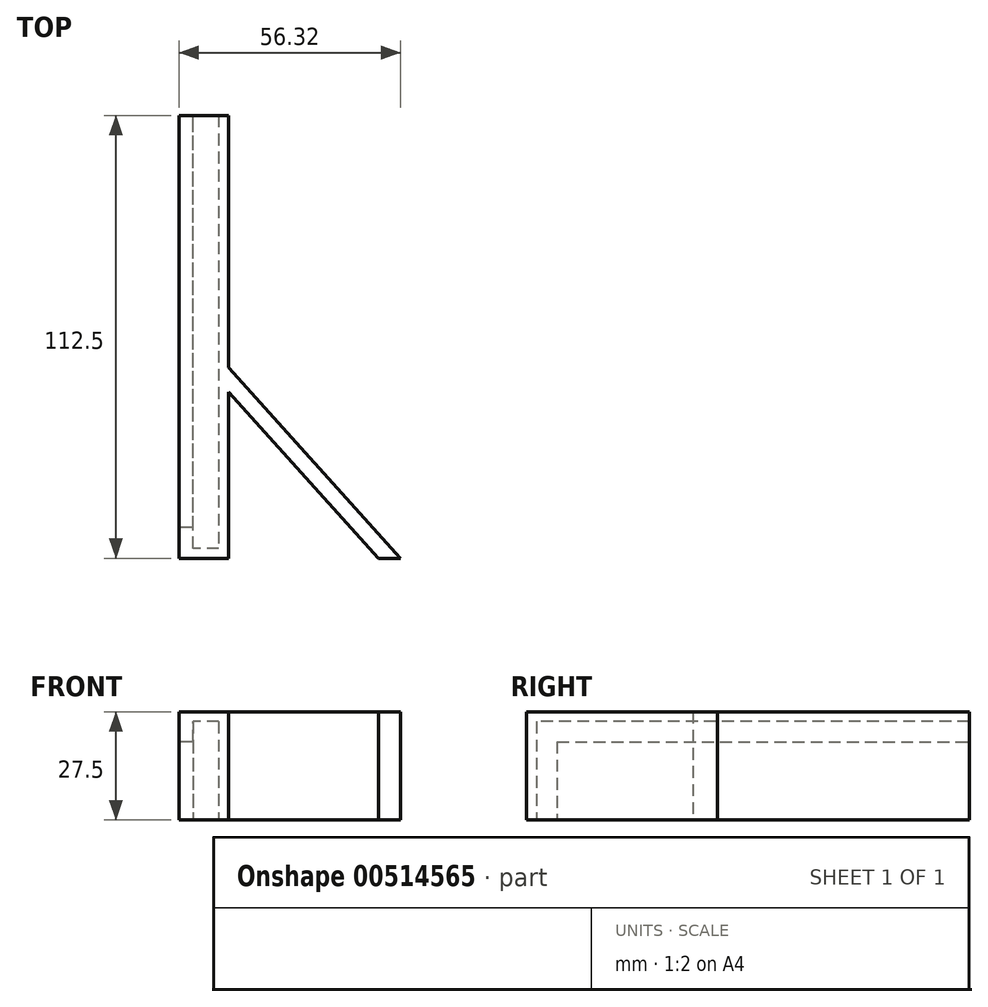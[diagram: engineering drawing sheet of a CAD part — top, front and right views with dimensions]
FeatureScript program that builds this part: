
annotation { "Feature Type Name" : "Feature", "Feature Type Description" : "" }
export const myFeature = defineFeature(function(context is Context, id is Id, definition is map)
    precondition{}
    {
        {
            var Q0;
            Q0=qCreatedBy(makeId("Top.planeOp"),FACE);
            var sketch = newSketch(context, id + "F0", { "sketchPlane" : qUnion([Q0])});
            skLineSegment(sketch, "E0", {"start": v(-21.92, -50.04) * mm, "end": v(-25.53, -50.04) * mm});
            skLineSegment(sketch, "E1", {"start": v(-25.53, -50.04) * mm, "end": v(-25.53, -57.84) * mm});
            skLineSegment(sketch, "E2", {"start": v(-25.53, -57.84) * mm, "end": v(-12.92, -57.84) * mm});
            skLineSegment(sketch, "E3", {"start": v(-12.92, -57.84) * mm, "end": v(-12.92, 34.29) * mm});
            skLineSegment(sketch, "E4", {"start": v(-12.92, 34.29) * mm, "end": v(-12.92, 54.66) * mm});
            skLineSegment(sketch, "E5", {"start": v(-12.92, 54.66) * mm, "end": v(-15.42, 54.66) * mm});
            skLineSegment(sketch, "E6", {"start": v(-15.42, 54.66) * mm, "end": v(-15.42, -55.34) * mm});
            skLineSegment(sketch, "E7", {"start": v(-15.42, -55.34) * mm, "end": v(-21.45, -55.34) * mm});
            skLineSegment(sketch, "E8", {"start": v(-21.45, -55.34) * mm, "end": v(-21.92, -55.34) * mm});
            skLineSegment(sketch, "E9", {"start": v(-21.92, -55.34) * mm, "end": v(-21.92, -50.04) * mm});
            skLineSegment(sketch, "E10", {"start": v(-12.92, -9.37) * mm, "end": v(30.79, -57.84) * mm});
            skLineSegment(sketch, "E11", {"start": v(30.79, -57.84) * mm, "end": v(25.16, -57.84) * mm});
            skLineSegment(sketch, "E12", {"start": v(25.16, -57.84) * mm, "end": v(-12.92, -15.62) * mm});
            skSolve(sketch);
        }
        {
            var Q0;
            Q0=makeQuery(id+"F0.imprint","IMPRINT",FACE,{"disambiguationData":[TD([[makeQuery(id+"F0.imprint","IMPRINT",EDGE,{"derivedFrom":sQuery(id+"F0.wireOp",EDGE,"E0")}),1.0]])]});
            var Q1;
            {var subQ0=sQuery(id+"F0.wireOp",EDGE,"E10");Q1=makeQuery(id+"F0.imprint","IMPRINT",FACE,{"disambiguationData":[TD([[makeQuery(id+"F0.imprint","IMPRINT",EDGE,{"derivedFrom":subQ0}),-1.0]])]});}
            extrude(context, id + "F1", {"entities" : qUnion([Q0, Q1]), "depth" : 25 * mm});
        }
        {
            var Q0;
            Q0=makeQuery(id+"F1.opExtrude","CAP_FACE",FACE,{"disambiguationData":[OSD([sQuery(id+"F0.wireOp",EDGE,"E0"),sQuery(id+"F0.wireOp",EDGE,"E1"),sQuery(id+"F0.wireOp",EDGE,"E2"),sQuery(id+"F0.wireOp",EDGE,"E3"),sQuery(id+"F0.wireOp",EDGE,"E4"),sQuery(id+"F0.wireOp",EDGE,"E5"),sQuery(id+"F0.wireOp",EDGE,"E6"),sQuery(id+"F0.wireOp",EDGE,"E7"),sQuery(id+"F0.wireOp",EDGE,"E8"),sQuery(id+"F0.wireOp",EDGE,"E9"),sQuery(id+"F0.wireOp",EDGE,"E10"),sQuery(id+"F0.wireOp",EDGE,"E11"),sQuery(id+"F0.wireOp",EDGE,"E12")])],"isStart":false});
            var sketch = newSketch(context, id + "F2", { "sketchPlane" : qUnion([Q0])});
            skLineSegment(sketch, "E13.bottom", {"start": v(-12.92, 54.66) * mm, "end": v(-25.53, 54.66) * mm});
            skLineSegment(sketch, "E13.top", {"start": v(-12.92, -57.84) * mm, "end": v(-25.53, -57.84) * mm});
            skLineSegment(sketch, "E13.left", {"start": v(-12.92, 54.66) * mm, "end": v(-12.92, -57.84) * mm});
            skLineSegment(sketch, "E13.right", {"start": v(-25.53, 54.66) * mm, "end": v(-25.53, -57.84) * mm});
            skSolve(sketch);
        }
        {
            var Q0;
            {var subQ1=makeQuery(id+"F1.opExtrude","CAP_EDGE",EDGE,{"disambiguationData":[OSD([sQuery(id+"F0.wireOp",EDGE,"E0")])],"isStart":false});Q0=makeQuery(id+"F2.imprint","IMPRINT",FACE,{"disambiguationData":[TD([[makeQuery(id+"F2.imprint","IMPRINT",EDGE,{"derivedFrom":subQ1}),-1.0]])]});}
            var Q1;
            {var subQ4=sQuery(id+"F2.wireOp",EDGE,"E13.top");Q1=makeQuery(id+"F2.imprint","IMPRINT",FACE,{"disambiguationData":[TD([[makeQuery(id+"F2.imprint","IMPRINT",EDGE,{"derivedFrom":subQ4}),1.0]])]});}
            extrude(context, id + "F3", {"entities" : qUnion([Q0, Q1]), "operationType" : NewBodyOperationType.ADD, "depth" : 2.5 * mm});
        }
        {
            var Q0;
            Q0=makeQuery(id+"F3.opExtrude","CAP_FACE",FACE,{"disambiguationData":[OSD([sQuery(id+"F2.wireOp",EDGE,"E13.bottom"),sQuery(id+"F2.wireOp",EDGE,"E13.top"),sQuery(id+"F2.wireOp",EDGE,"E13.left"),sQuery(id+"F2.wireOp",EDGE,"E13.right")])],"isStart":true});
            var sketch = newSketch(context, id + "F4", { "sketchPlane" : qUnion([Q0])});
            skLineSegment(sketch, "E14.bottom", {"start": v(-25.53, 50.04) * mm, "end": v(-21.92, 50.04) * mm});
            skLineSegment(sketch, "E14.top", {"start": v(-25.53, -54.66) * mm, "end": v(-21.92, -54.66) * mm});
            skLineSegment(sketch, "E14.left", {"start": v(-25.53, 50.04) * mm, "end": v(-25.53, -54.66) * mm});
            skLineSegment(sketch, "E14.right", {"start": v(-21.92, 50.04) * mm, "end": v(-21.92, -54.66) * mm});
            skSolve(sketch);
        }
        {
            var Q0;
            Q0=makeQuery(id+"F4.imprint","IMPRINT",FACE,{"disambiguationData":[TD([[makeQuery(id+"F4.imprint","IMPRINT",EDGE,{"derivedFrom":sQuery(id+"F4.wireOp",EDGE,"E14.bottom")}),1.0]])]});
            extrude(context, id + "F5", {"entities" : qUnion([Q0]), "operationType" : NewBodyOperationType.ADD, "depth" : 5.1 * mm});
        }
        {
            var Q0;
            Q0=makeQuery(id+"F1.opExtrude","CAP_FACE",FACE,{"disambiguationData":[OSD([sQuery(id+"F0.wireOp",EDGE,"E0"),sQuery(id+"F0.wireOp",EDGE,"E1"),sQuery(id+"F0.wireOp",EDGE,"E2"),sQuery(id+"F0.wireOp",EDGE,"E3"),sQuery(id+"F0.wireOp",EDGE,"E4"),sQuery(id+"F0.wireOp",EDGE,"E5"),sQuery(id+"F0.wireOp",EDGE,"E6"),sQuery(id+"F0.wireOp",EDGE,"E7"),sQuery(id+"F0.wireOp",EDGE,"E8"),sQuery(id+"F0.wireOp",EDGE,"E9"),sQuery(id+"F0.wireOp",EDGE,"E10"),sQuery(id+"F0.wireOp",EDGE,"E11"),sQuery(id+"F0.wireOp",EDGE,"E12")])],"isStart":false});
            var Q1;
            Q1=makeQuery(id+"F3.opExtrude","CAP_FACE",FACE,{"disambiguationData":[OSD([sQuery(id+"F2.wireOp",EDGE,"E13.bottom"),sQuery(id+"F2.wireOp",EDGE,"E13.top"),sQuery(id+"F2.wireOp",EDGE,"E13.left"),sQuery(id+"F2.wireOp",EDGE,"E13.right")])],"isStart":false});
            extrude(context, id + "F6", {"entities" : qUnion([Q0]), "operationType" : NewBodyOperationType.ADD, "endBound" : BoundingType.UP_TO_SURFACE, "endBoundEntityFace" : qUnion([Q1]), "depth" : 25 * mm});
        }
    });
